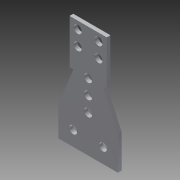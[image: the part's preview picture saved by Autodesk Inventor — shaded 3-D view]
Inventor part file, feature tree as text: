
AUTODESK INVENTOR PART (.ipt)
format: ipt  version: 2013 (Build 170138000, 138)  size: 140,800 bytes
history: native  units: in
note: dims shown in document units (in); Inventor stores cm internally (conversion verified against a paired STEP export)
features: extrude x6, sketch x6, reference x5
ambient origin geometry x8: Origin, YZ Plane, XZ Plane, XY Plane, X Axis, Y Axis, Z Axis, Center Point
bodies: Solid1 (feature_tree)
feature tree (17):
  extrude  "Extrusion1"  Depth=2.25in
  extrude  "Extrusion2"  Depth=0.5in
  extrude  "Extrusion3"  Depth=0.125in TaperAngle=0.0deg
  extrude  "Extrusion4"  Depth=0.125in TaperAngle=0.0deg
  extrude  "Extrusion5"  Depth=0.15in
  extrude  "Extrusion6"  Depth=0.5in
  sketch  "Sketch1"  dims[d0=2.0in d1=2.25in]
  sketch  "Sketch2"  dims[d2=1.0in d3=0.5in]
  sketch  "Sketch3"  dims[d4=0.5in d5=0.125in d6=0.0in]
  reference  "Reference1"
  reference  "Reference2"
  reference  "Reference3"
  reference  "Reference4"
  reference  "Reference5"
  sketch  "Sketch4"  dims[d7=1.5in d8=0.125in d9=0.0in]
  sketch  "Sketch5"  dims[d10=0.125in d11=0.0in d12=0.15in]
  sketch  "Sketch6"  dims[d13=0.25in d14=0.5in d15=0.15in d16=0.266in d17=0.266in d18=0.266in d19=0.266in d20=1.0in d21=0.0in d22=0.125in d23=0.0in d24=0.125in d25=0.0in]
